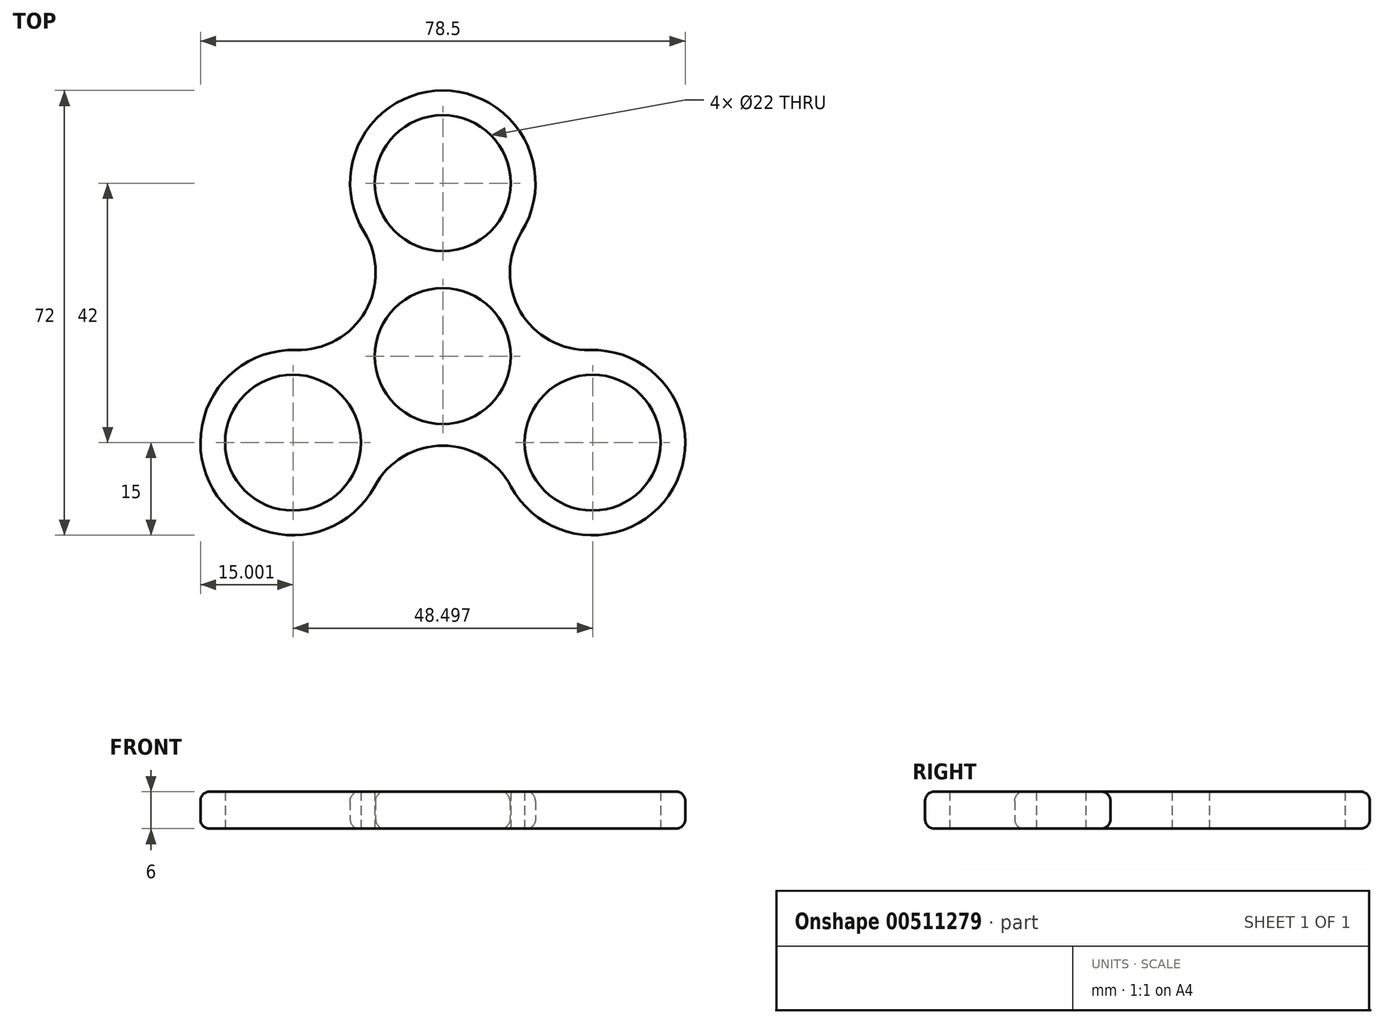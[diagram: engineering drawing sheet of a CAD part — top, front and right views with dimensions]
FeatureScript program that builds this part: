
annotation { "Feature Type Name" : "Feature", "Feature Type Description" : "" }
export const myFeature = defineFeature(function(context is Context, id is Id, definition is map)
    precondition{}
    {
        {
            var Q0;
            Q0=qCreatedBy(makeId("Top.planeOp"),FACE);
            var sketch = newSketch(context, id + "F0", { "sketchPlane" : qUnion([Q0])});
            skLineSegment(sketch, "E0", {"start": v(0, 0) * mm, "end": v(0, 64.89) * mm, "construction": true});
            skLineSegment(sketch, "E1", {"start": v(0, 0) * mm, "end": v(61.7, -35.63) * mm, "construction": true});
            skLineSegment(sketch, "E2", {"start": v(0, 0) * mm, "end": v(-64.28, -37.1) * mm, "construction": true});
            skPoint(sketch, "E3", {"position": v(0, 28) * mm});
            skPoint(sketch, "E4", {"position": v(24.25, -14) * mm});
            skPoint(sketch, "E5", {"position": v(-24.25, -14) * mm});
            skCircle(sketch, "E6", {"center": v(0, 28) * mm, "radius": 11 * mm});
            skCircle(sketch, "E7", {"center": v(24.25, -14) * mm, "radius": 11 * mm});
            skCircle(sketch, "E8", {"center": v(-24.25, -14) * mm, "radius": 11 * mm});
            skCircle(sketch, "E9", {"center": v(0, 0) * mm, "radius": 11 * mm});
            skCircle(sketch, "E10", {"center": v(0, 28) * mm, "radius": 15 * mm});
            skCircle(sketch, "E11", {"center": v(24.25, -14) * mm, "radius": 15 * mm});
            skCircle(sketch, "E12", {"center": v(-24.25, -14) * mm, "radius": 15 * mm});
            skLineSegment(sketch, "E13", {"start": v(0, 0) * mm, "end": v(-65.71, 37.94) * mm, "construction": true});
            skLineSegment(sketch, "E14", {"start": v(0, 0) * mm, "end": v(0, -59.6) * mm, "construction": true});
            skLineSegment(sketch, "E15", {"start": v(0, 0) * mm, "end": v(69.4, 40.06) * mm, "construction": true});
            skPoint(sketch, "E16", {"position": v(-23.38, 13.5) * mm});
            skPoint(sketch, "E17", {"position": v(0, -27) * mm});
            skPoint(sketch, "E18", {"position": v(23.38, 13.5) * mm});
            skCircle(sketch, "E19", {"center": v(-23.38, 13.5) * mm, "radius": 12.51 * mm});
            skCircle(sketch, "E20", {"center": v(0, -27) * mm, "radius": 12.51 * mm});
            skCircle(sketch, "E21", {"center": v(23.38, 13.5) * mm, "radius": 12.51 * mm});
            skSolve(sketch);
        }
        {
            var Q0;
            Q0=makeQuery(id+"F0.imprint","IMPRINT",FACE,{"disambiguationData":[TD([[makeQuery(id+"F0.imprint","IMPRINT",EDGE,{"derivedFrom":sQuery(id+"F0.wireOp",EDGE,"E6")}),-1.0]])]});
            var Q1;
            Q1=makeQuery(id+"F0.imprint","IMPRINT",FACE,{"disambiguationData":[TD([[makeQuery(id+"F0.imprint","IMPRINT",EDGE,{"derivedFrom":sQuery(id+"F0.wireOp",EDGE,"E9")}),-1.0]])]});
            var Q2;
            Q2=makeQuery(id+"F0.imprint","IMPRINT",FACE,{"disambiguationData":[TD([[makeQuery(id+"F0.imprint","IMPRINT",EDGE,{"derivedFrom":sQuery(id+"F0.wireOp",EDGE,"E8")}),-1.0]])]});
            var Q3;
            Q3=makeQuery(id+"F0.imprint","IMPRINT",FACE,{"disambiguationData":[TD([[makeQuery(id+"F0.imprint","IMPRINT",EDGE,{"derivedFrom":sQuery(id+"F0.wireOp",EDGE,"E7")}),-1.0]])]});
            extrude(context, id + "F1", {"entities" : qUnion([Q0, Q1, Q2, Q3]), "depth" : 6 * mm});
        }
        {
            var Q0;
            Q0=makeQuery(id+"F1.opExtrude","CAP_EDGE",EDGE,{"disambiguationData":[OSD([sQuery(id+"F0.wireOp",EDGE,"E19")])],"isStart":false});
            var Q1;
            Q1=makeQuery(id+"F1.opExtrude","CAP_EDGE",EDGE,{"disambiguationData":[OSD([sQuery(id+"F0.wireOp",EDGE,"E12")])],"isStart":true});
            fillet(context, id + "F2", {"entities" : qUnion([Q0, Q1]), "radius" : 1.5 * mm, "tangentPropagation" : true, "allowEdgeOverflow" : false});
        }
    });
